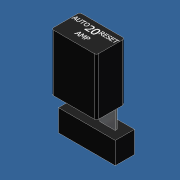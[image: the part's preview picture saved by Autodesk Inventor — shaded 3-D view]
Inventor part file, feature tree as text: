
AUTODESK INVENTOR PART (.ipt)
format: ipt  version: 2012 (Build 160160000, 160)  size: 332,800 bytes
history: native  units: mm (DEFAULTED — no unit token found)
features: extrude x4, sketch x4, plane x3
ambient origin geometry x5: Origin, X Axis, Y Axis, Z Axis, Center Point
bodies: Solid1 (feature_tree)
feature tree (11):
  extrude  "Extrusion1"  Depth=9.906mm
  extrude  "Extrusion2"  Depth=19.812mm TaperAngle=0.0deg
  extrude  "Extrusion3"  Depth=5.3848mm
  extrude  "Extrusion4"  Depth=2.9718mm
  plane  "YZ Plane (RIGHT)"
  plane  "XZ Plane (TOP)"
  plane  "XY Plane (FRONT)"
  sketch  "Sketch2"  dims[d0=15.748mm d1=9.906mm]
  sketch  "Sketch3"  dims[d2=0.762mm d3=19.812mm d4=0.0mm]
  sketch  "Sketch4"  dims[d5=0.7112mm d6=5.3848mm]
  sketch  "Sketch5"  dims[d7=7.874mm d8=2.9718mm d9=14.478mm d10=0.0mm d11=34.6964mm d12=6.7056mm d13=7.62mm d14=19.812mm d15=0.0mm d16=0.00254mm d17=0.0mm]
